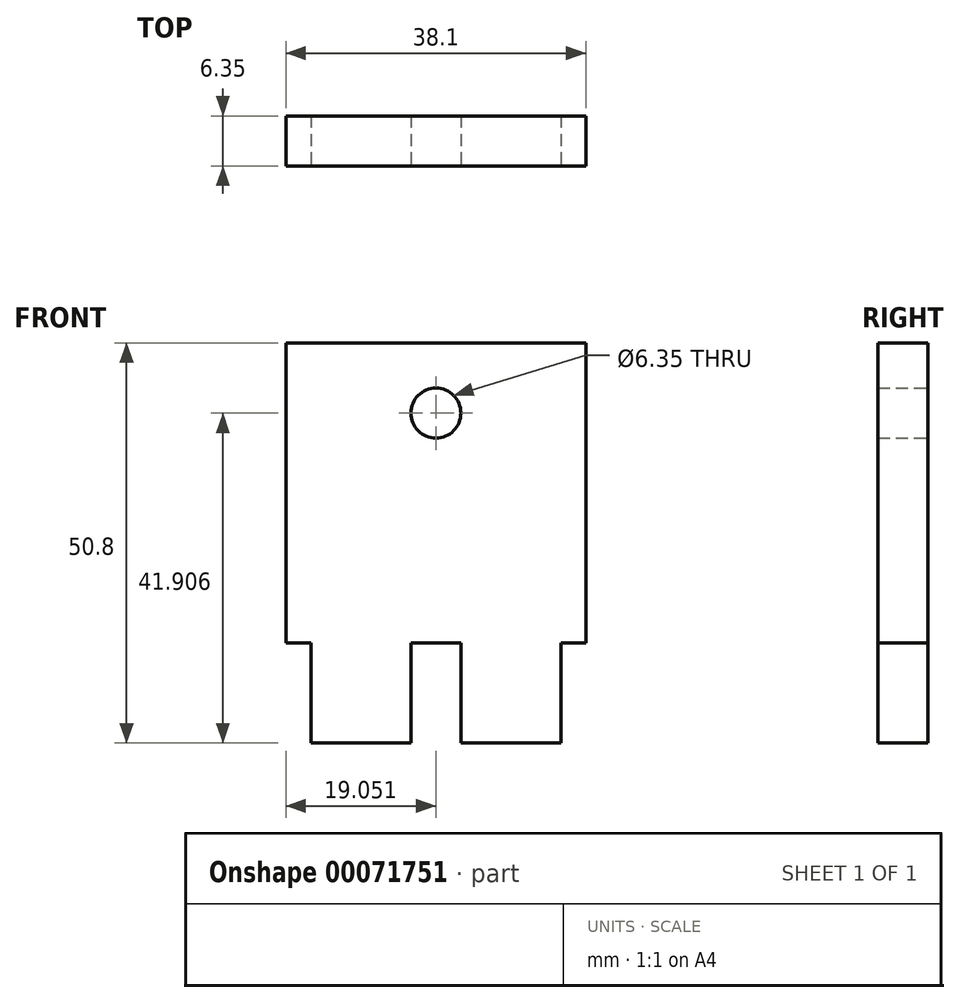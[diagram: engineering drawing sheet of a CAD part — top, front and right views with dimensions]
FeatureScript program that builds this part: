
annotation { "Feature Type Name" : "Feature", "Feature Type Description" : "" }
export const myFeature = defineFeature(function(context is Context, id is Id, definition is map)
    precondition{}
    {
        {
            var Q0;
            Q0=qCreatedBy(makeId("Front.planeOp"),FACE);
            var sketch = newSketch(context, id + "F0", { "sketchPlane" : qUnion([Q0])});
            skLineSegment(sketch, "E0.bottom", {"start": v(-20.36, 57.34) * mm, "end": v(17.74, 57.34) * mm});
            skLineSegment(sketch, "E0.top", {"start": v(-20.36, 6.54) * mm, "end": v(17.74, 6.54) * mm});
            skLineSegment(sketch, "E0.left", {"start": v(-20.36, 57.34) * mm, "end": v(-20.36, 6.54) * mm});
            skLineSegment(sketch, "E0.right", {"start": v(17.74, 57.34) * mm, "end": v(17.74, 6.54) * mm});
            skSolve(sketch);
        }
        {
            var Q0;
            Q0 = qSketchRegion(id + "F0", true);
            extrude(context, id + "F1", {"entities" : qUnion([Q0]), "depth" : 6.35 * mm});
        }
        {
            var Q0;
            Q0=makeQuery(id+"F1.opExtrude","CAP_FACE",FACE,{"disambiguationData":[OSD([sQuery(id+"F0.wireOp",EDGE,"E0.bottom"),sQuery(id+"F0.wireOp",EDGE,"E0.top"),sQuery(id+"F0.wireOp",EDGE,"E0.left"),sQuery(id+"F0.wireOp",EDGE,"E0.right")])],"isStart":true});
            var sketch = newSketch(context, id + "F2", { "sketchPlane" : qUnion([Q0])});
            skLineSegment(sketch, "E1", {"start": v(1.3, 6.54) * mm, "end": v(1.3, 57.34) * mm, "construction": true});
            skLineSegment(sketch, "E2", {"start": v(-17.74, 48.45) * mm, "end": v(20.36, 48.45) * mm, "construction": true});
            skCircle(sketch, "E3", {"center": v(1.3, 48.45) * mm, "radius": 3.18 * mm});
            skSolve(sketch);
        }
        {
            var Q0;
            Q0 = qSketchRegion(id + "F2", true);
            extrude(context, id + "F3", {"entities" : qUnion([Q0]), "operationType" : NewBodyOperationType.REMOVE, "endBound" : BoundingType.THROUGH_ALL, "oppositeDirection" : true, "depth" : 25.4 * mm});
        }
        {
            var Q0;
            Q0=makeQuery(id+"F1.opExtrude","CAP_FACE",FACE,{"disambiguationData":[OSD([sQuery(id+"F0.wireOp",EDGE,"E0.bottom"),sQuery(id+"F0.wireOp",EDGE,"E0.top"),sQuery(id+"F0.wireOp",EDGE,"E0.left"),sQuery(id+"F0.wireOp",EDGE,"E0.right")])],"isStart":false});
            var sketch = newSketch(context, id + "F4", { "sketchPlane" : qUnion([Q0])});
            skLineSegment(sketch, "E4.bottom", {"start": v(-20.36, 19.24) * mm, "end": v(-17.18, 19.24) * mm});
            skLineSegment(sketch, "E4.top", {"start": v(-20.36, 6.54) * mm, "end": v(-17.18, 6.54) * mm});
            skLineSegment(sketch, "E4.left", {"start": v(-20.36, 19.24) * mm, "end": v(-20.36, 6.54) * mm});
            skLineSegment(sketch, "E4.right", {"start": v(-17.18, 19.24) * mm, "end": v(-17.18, 6.54) * mm});
            skLineSegment(sketch, "E5.bottom", {"start": v(17.74, 19.24) * mm, "end": v(14.57, 19.24) * mm});
            skLineSegment(sketch, "E5.top", {"start": v(17.74, 6.54) * mm, "end": v(14.57, 6.54) * mm});
            skLineSegment(sketch, "E5.left", {"start": v(17.74, 19.24) * mm, "end": v(17.74, 6.54) * mm});
            skLineSegment(sketch, "E5.right", {"start": v(14.57, 19.24) * mm, "end": v(14.57, 6.54) * mm});
            skSolve(sketch);
        }
        {
            var Q0;
            Q0 = qSketchRegion(id + "F4", true);
            extrude(context, id + "F5", {"entities" : qUnion([Q0]), "operationType" : NewBodyOperationType.REMOVE, "endBound" : BoundingType.THROUGH_ALL, "oppositeDirection" : true, "depth" : 25.4 * mm});
        }
        {
            var Q0;
            Q0=makeQuery(id+"F1.opExtrude","CAP_FACE",FACE,{"disambiguationData":[OSD([sQuery(id+"F0.wireOp",EDGE,"E0.bottom"),sQuery(id+"F0.wireOp",EDGE,"E0.top"),sQuery(id+"F0.wireOp",EDGE,"E0.left"),sQuery(id+"F0.wireOp",EDGE,"E0.right")])],"isStart":false});
            var sketch = newSketch(context, id + "F6", { "sketchPlane" : qUnion([Q0])});
            skLineSegment(sketch, "E6", {"start": v(-1.3, 57.34) * mm, "end": v(-1.3, 6.54) * mm, "construction": true});
            skLineSegment(sketch, "E7.bottom", {"start": v(-4.48, 6.54) * mm, "end": v(1.87, 6.54) * mm});
            skLineSegment(sketch, "E7.top", {"start": v(-4.48, 19.24) * mm, "end": v(1.87, 19.24) * mm});
            skLineSegment(sketch, "E7.left", {"start": v(-4.48, 6.54) * mm, "end": v(-4.48, 19.24) * mm});
            skLineSegment(sketch, "E7.right", {"start": v(1.87, 6.54) * mm, "end": v(1.87, 19.24) * mm});
            skSolve(sketch);
        }
        {
            var Q0;
            Q0 = qSketchRegion(id + "F6", true);
            extrude(context, id + "F7", {"entities" : qUnion([Q0]), "operationType" : NewBodyOperationType.REMOVE, "endBound" : BoundingType.THROUGH_ALL, "oppositeDirection" : true, "depth" : 25.4 * mm});
        }
    });
